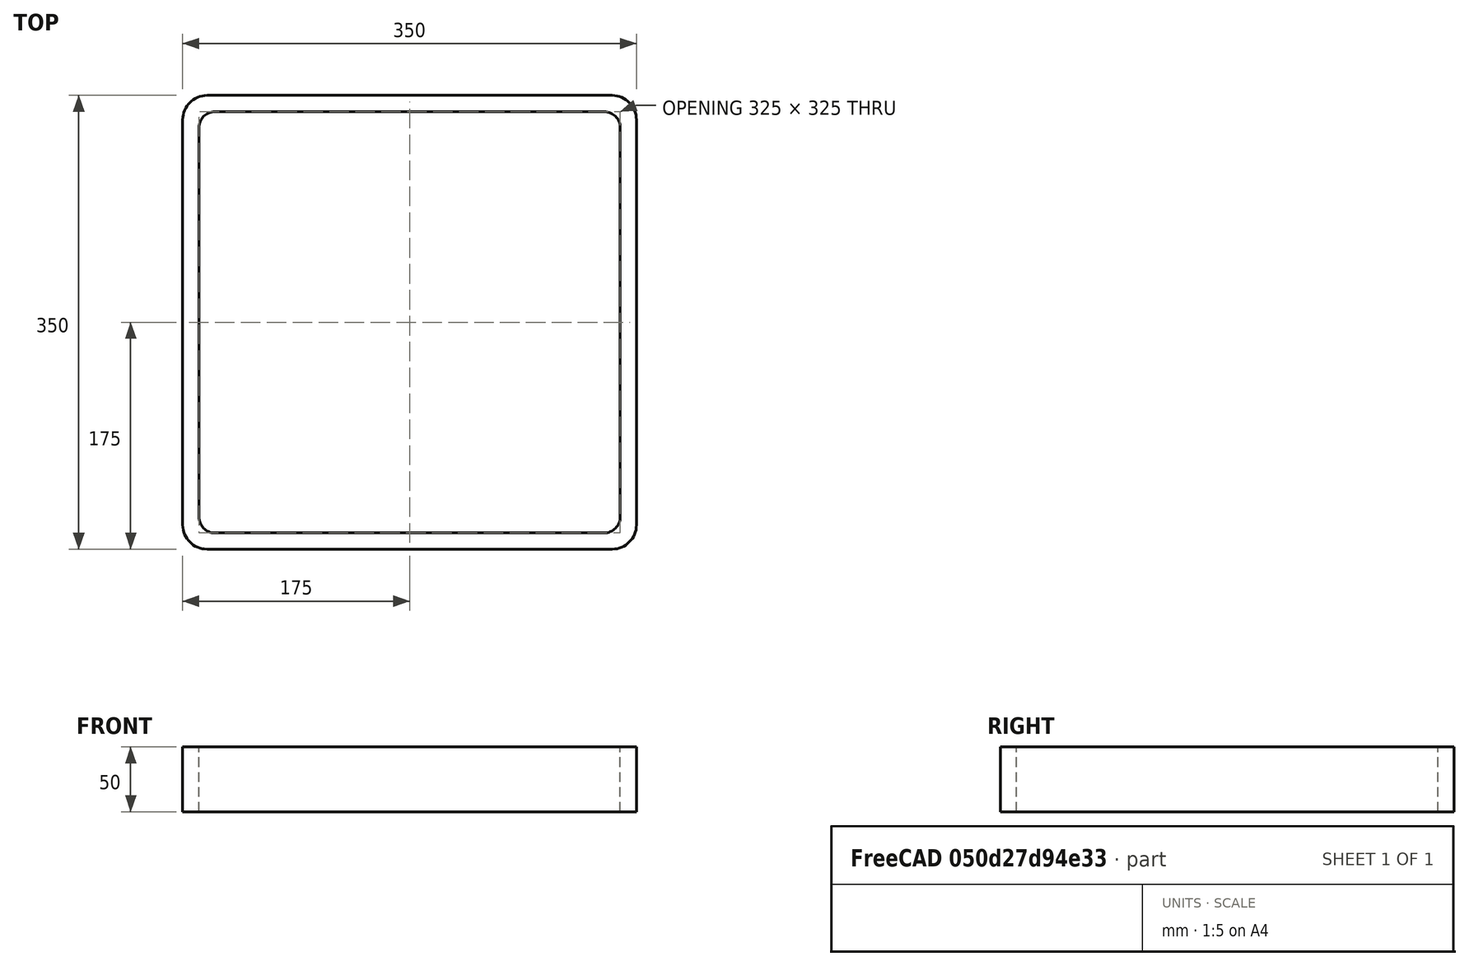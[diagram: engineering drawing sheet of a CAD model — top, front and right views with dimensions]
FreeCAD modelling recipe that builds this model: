
FCSTD DOCUMENT  (FreeCAD 0.15R4671 (Git))
Label: Square hollow section 350x350x12.5 EN10219 S235JRH
License: All rights reserved
LicenseURL: http://en.wikipedia.org/wiki/All_rights_reserved
objects: Sketcher::SketchObject×1, Part::Extrusion×1
note: 2 computed .brp shape members not serialized (recipe doc carries the construction recipe); baked Part::Feature solids carry a one-line shape summary decoded from their .brp

FEATURE [Sketcher::SketchObject] Sketch
  sketch-geometry (16):
    g0: LineSegment StartX=-150 StartY=162.5 StartZ=0 EndX=150 EndY=162.5 EndZ=0
    g1: LineSegment StartX=162.5 StartY=150 StartZ=0 EndX=162.5 EndY=-150 EndZ=0
    g2: LineSegment StartX=150 StartY=-162.5 StartZ=0 EndX=-150 EndY=-162.5 EndZ=0
    g3: LineSegment StartX=-162.5 StartY=-150 StartZ=0 EndX=-162.5 EndY=150 EndZ=0
    g4: LineSegment StartX=-156.25 StartY=175 StartZ=0 EndX=156.25 EndY=175 EndZ=0
    g5: LineSegment StartX=175 StartY=156.25 StartZ=0 EndX=175 EndY=-156.25 EndZ=0
    g6: LineSegment StartX=156.25 StartY=-175 StartZ=0 EndX=-156.25 EndY=-175 EndZ=0
    g7: LineSegment StartX=-175 StartY=-156.25 StartZ=0 EndX=-175 EndY=156.25 EndZ=0
    g8: ArcOfCircle CenterX=-150 CenterY=150 CenterZ=0 NormalX=0 NormalY=0 NormalZ=1 Radius=12.5 StartAngle=1.5708 EndAngle=3.14159
    g9: ArcOfCircle CenterX=150 CenterY=150 CenterZ=0 NormalX=0 NormalY=0 NormalZ=1 Radius=12.5 StartAngle=0 EndAngle=1.5708
    g10: ArcOfCircle CenterX=150 CenterY=-150 CenterZ=0 NormalX=0 NormalY=0 NormalZ=1 Radius=12.5 StartAngle=4.71239 EndAngle=6.28319
    g11: ArcOfCircle CenterX=-150 CenterY=-150 CenterZ=0 NormalX=0 NormalY=0 NormalZ=1 Radius=12.5 StartAngle=3.14159 EndAngle=4.71239
    g12: ArcOfCircle CenterX=156.25 CenterY=156.25 CenterZ=0 NormalX=0 NormalY=0 NormalZ=1 Radius=18.75 StartAngle=0 EndAngle=1.5708
    g13: ArcOfCircle CenterX=156.25 CenterY=-156.25 CenterZ=0 NormalX=0 NormalY=0 NormalZ=1 Radius=18.75 StartAngle=4.71239 EndAngle=6.28319
    g14: ArcOfCircle CenterX=-156.25 CenterY=-156.25 CenterZ=0 NormalX=0 NormalY=0 NormalZ=1 Radius=18.75 StartAngle=3.14159 EndAngle=4.71239
    g15: ArcOfCircle CenterX=-156.25 CenterY=156.25 CenterZ=0 NormalX=0 NormalY=0 NormalZ=1 Radius=18.75 StartAngle=1.5708 EndAngle=3.14159
  constraints (36):
    c: Horizontal(g2)
    c: Vertical(g3)
    c: Horizontal(g6)
    c: Vertical(g7)
    c: Tangent(g3,g8) = 1.5708
    c: Tangent(g0,g8) = 1.5708
    c: Tangent(g0,g9) = 1.5708
    c: Tangent(g1,g9) = 1.5708
    c: Tangent(g1,g10) = 1.5708
    c: Tangent(g2,g10) = 1.5708
    c: Tangent(g2,g11) = 1.5708
    c: Tangent(g3,g11) = 1.5708
    c: Tangent(g4,g12) = 1.5708
    c: Tangent(g5,g12) = 1.5708
    c: Tangent(g5,g13) = 1.5708
    c: Tangent(g6,g13) = 1.5708
    c: Tangent(g6,g14) = 1.5708
    c: Tangent(g7,g14) = 1.5708
    c: Tangent(g7,g15) = 1.5708
    c: Tangent(g4,g15) = 1.5708
    c: Equal(g9,g8)
    c: Equal(g9,g11)
    c: Equal(g9,g10)
    c: Equal(g12,g15)
    c: Equal(g12,g14)
    c: Equal(g12,g13)
    c: Symmetric(g4,g6,g-1)
    c: Symmetric(g7,g5,g-2)
    c: DistanceY(g4,g6) = -350
    c: DistanceX(g7,g5) = 350
    c: Symmetric(g3,g1,g-2)
    c: Symmetric(g0,g2,g-1)
    c: DistanceY(g0,g4) = 12.5
    c: DistanceX(g5,g1) = -12.5
    c: Radius(g9) = 12.5
    c: Radius(g12) = 18.75
FEATURE [Part::Extrusion] Extrude  label="Square hollow section 350x350x12.5 EN10219 S235JRH"
  Base = -> Sketch
  Dir = (0,0,50)
  Solid = true
